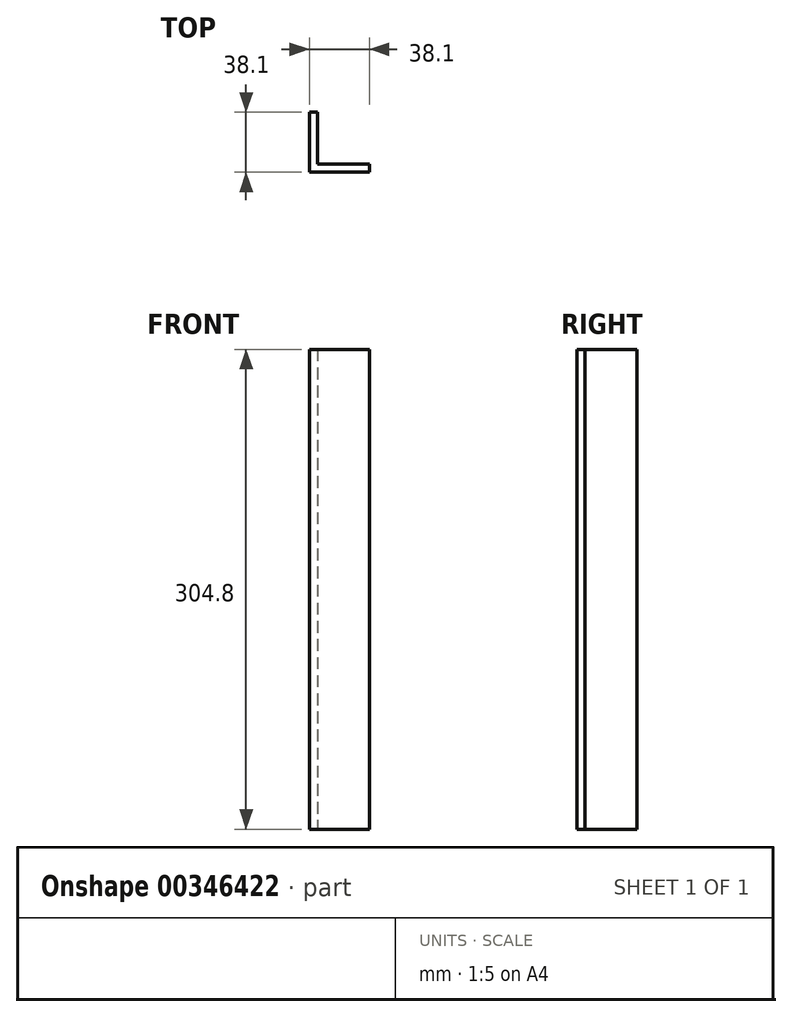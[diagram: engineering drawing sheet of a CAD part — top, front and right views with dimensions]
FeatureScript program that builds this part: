
annotation { "Feature Type Name" : "Feature", "Feature Type Description" : "" }
export const myFeature = defineFeature(function(context is Context, id is Id, definition is map)
    precondition{}
    {
        {
            var Q0;
            Q0=qCreatedBy(makeId("Top.planeOp"),FACE);
            var sketch = newSketch(context, id + "F0", { "sketchPlane" : qUnion([Q0])});
            skLineSegment(sketch, "E0.bottom", {"start": v(-49.46, 22.73) * mm, "end": v(-44.38, 22.73) * mm});
            skLineSegment(sketch, "E0.left", {"start": v(-49.46, 22.73) * mm, "end": v(-49.46, -10.29) * mm});
            skLineSegment(sketch, "E0.right", {"start": v(-44.38, 22.73) * mm, "end": v(-44.38, -10.29) * mm});
            skLineSegment(sketch, "E1.bottom", {"start": v(-44.38, -10.29) * mm, "end": v(-11.36, -10.29) * mm});
            skLineSegment(sketch, "E1.top", {"start": v(-49.46, -15.37) * mm, "end": v(-11.36, -15.37) * mm});
            skLineSegment(sketch, "E1.left", {"start": v(-49.46, -10.29) * mm, "end": v(-49.46, -15.37) * mm});
            skLineSegment(sketch, "E1.right", {"start": v(-11.36, -10.29) * mm, "end": v(-11.36, -15.37) * mm});
            skSolve(sketch);
        }
        {
            var Q0;
            Q0 = qSketchRegion(id + "F0", true);
            extrude(context, id + "F1", {"entities" : qUnion([Q0]), "depth" : 304.8 * mm});
        }
    });
